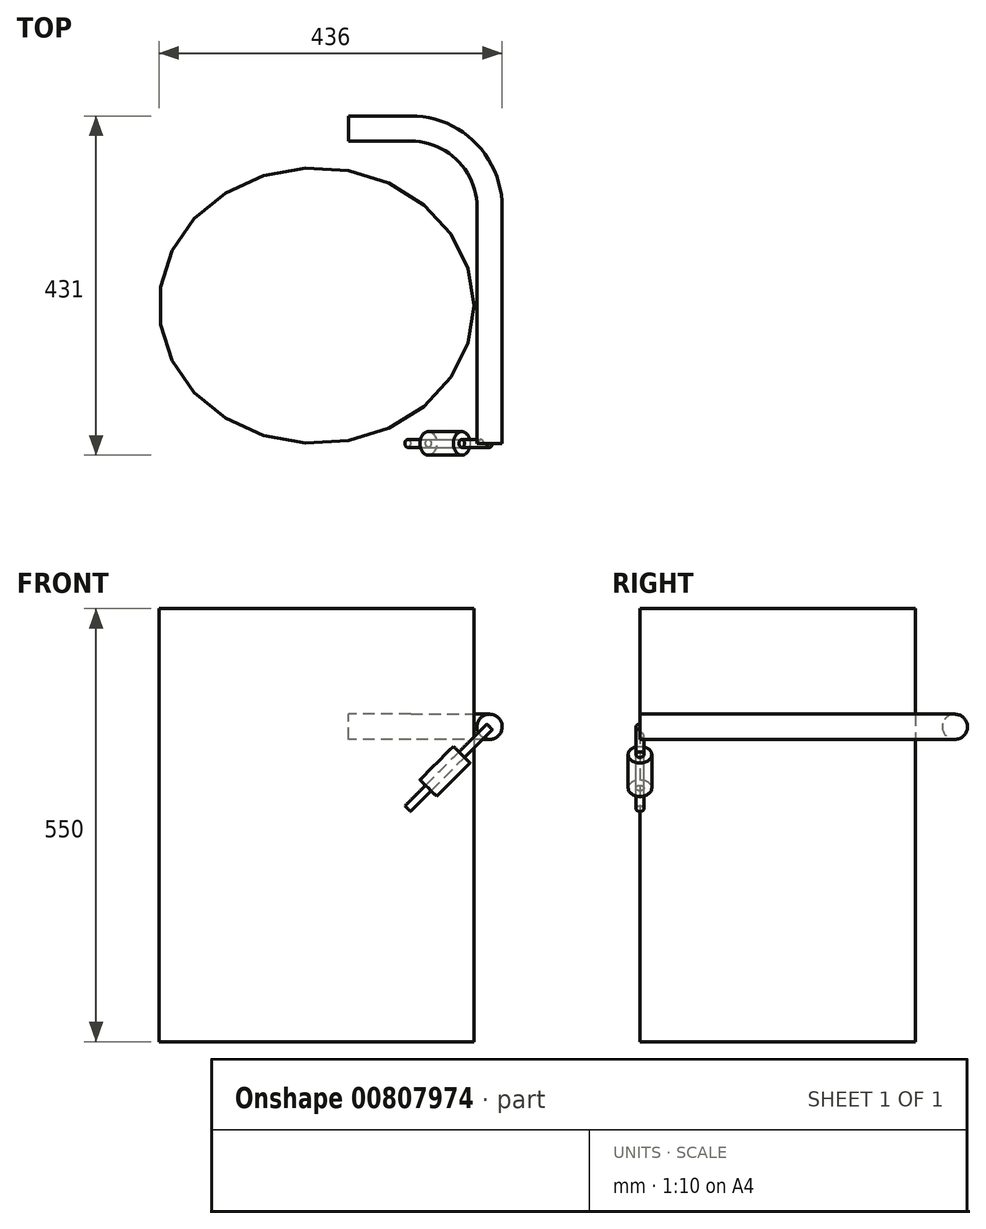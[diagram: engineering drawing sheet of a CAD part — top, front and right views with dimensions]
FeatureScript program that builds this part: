
annotation { "Feature Type Name" : "Feature", "Feature Type Description" : "" }
export const myFeature = defineFeature(function(context is Context, id is Id, definition is map)
    precondition{}
    {
        {
            var Q0;
            Q0=qCreatedBy(makeId("Top.planeOp"),FACE);
            var sketch = newSketch(context, id + "F0", { "sketchPlane" : qUnion([Q0])});
            skLineSegment(sketch, "E0", {"start": v(-179, 400) * mm, "end": v(-100, 400) * mm});
            skLineSegment(sketch, "E1", {"start": v(0, 0) * mm, "end": v(0, 300) * mm});
            skPoint(sketch, "E2.visualSharp", {"position": v(0, 400) * mm});
            skArc(sketch, "E2.filletArc", {"start": v(0, 300) * mm, "mid": v(-29.29, 370.71) * mm, "end": v(-100, 400) * mm});
            skSolve(sketch);
        }
        {
            var Q0;
            Q0=qCreatedBy(makeId("Front.planeOp"),FACE);
            var sketch = newSketch(context, id + "F1", { "sketchPlane" : qUnion([Q0])});
            skLineSegment(sketch, "E3", {"start": v(0, 0) * mm, "end": v(0, 117.2) * mm, "construction": true});
            skLineSegment(sketch, "E4", {"start": v(0, 0) * mm, "end": v(-104.01, -104.01) * mm});
            skSolve(sketch);
        }
        {
            var Q0;
            Q0=qCreatedBy(makeId("Front.planeOp"),FACE);
            var sketch = newSketch(context, id + "F2", { "sketchPlane" : qUnion([Q0])});
            skCircle(sketch, "E5", {"center": v(0, 0) * mm, "radius": 16 * mm});
            skSolve(sketch);
        }
        {
            var Q0;
            Q0=makeQuery(id+"F2.imprint","IMPRINT",FACE,{"disambiguationData":[TD([[makeQuery(id+"F2.imprint","IMPRINT",EDGE,{"derivedFrom":sQuery(id+"F2.wireOp",EDGE,"E5")}),1.0]])]});
            var Q1;
            Q1=sQuery(id+"F0.wireOp",EDGE,"E1");
            var Q2;
            Q2=sQuery(id+"F0.wireOp",EDGE,"E2.filletArc");
            var Q3;
            Q3=sQuery(id+"F0.wireOp",EDGE,"E0");
            sweep(context, id + "F3", {"profiles" : qUnion([Q0]), "path" : qUnion([Q1, Q2, Q3])});
        }
        {
            var Q0;
            Q0=sQuery(id+"F1.wireOp",EDGE,"E4");
            var Q1;
            Q1=sQuery(id+"F1.wireOp",VERTEX,"E3.start");
            cPlane(context, id + "F4", {"entities" : qUnion([Q0, Q1]), "cplaneType" : CPlaneType.LINE_POINT, "offset" : 25 * mm, "width" : 150 * mm, "height" : 150 * mm});
        }
        {
            var Q0;
            Q0=qCreatedBy(id+"F4.planeOp",FACE);
            var sketch = newSketch(context, id + "F5", { "sketchPlane" : qUnion([Q0])});
            skCircle(sketch, "E6", {"center": v(0, 0) * mm, "radius": 5 * mm});
            skSolve(sketch);
        }
        {
            var Q0;
            Q0 = qSketchRegion(id + "F5", true);
            var Q1;
            Q1=sQuery(id+"F1.wireOp",VERTEX,"E4.end");
            extrude(context, id + "F6", {"entities" : qUnion([Q0]), "operationType" : NewBodyOperationType.ADD, "endBound" : BoundingType.UP_TO_VERTEX, "depth" : 25 * mm, "endBoundEntityVertex" : qUnion([Q1]), "offsetDistance" : 25 * mm});
        }
        {
            var Q0;
            Q0=qCreatedBy(id+"F4.planeOp",FACE);
            cPlane(context, id + "F7", {"entities" : qUnion([Q0]), "cplaneType" : CPlaneType.OFFSET, "offset" : 50 * mm, "width" : 150 * mm, "height" : 150 * mm});
        }
        {
            var Q0;
            Q0=qCreatedBy(id+"F7.planeOp",FACE);
            var sketch = newSketch(context, id + "F8", { "sketchPlane" : qUnion([Q0])});
            skCircle(sketch, "E7", {"center": v(0, 0) * mm, "radius": 15 * mm});
            skCircle(sketch, "E8", {"center": v(0, 0) * mm, "radius": 5 * mm});
            skSolve(sketch);
        }
        {
            var Q0;
            Q0=makeQuery(id+"F8.imprint","IMPRINT",FACE,{"disambiguationData":[TD([[makeQuery(id+"F8.imprint","IMPRINT",EDGE,{"derivedFrom":sQuery(id+"F8.wireOp",EDGE,"E7")}),1.0]])]});
            extrude(context, id + "F9", {"entities" : qUnion([Q0]), "depth" : 60 * mm, "offsetDistance" : 25 * mm});
        }
        {
            var Q0;
            Q0=qCreatedBy(makeId("Top.planeOp"),FACE);
            var sketch = newSketch(context, id + "F10", { "sketchPlane" : qUnion([Q0])});
            skLineSegment(sketch, "E9", {"start": v(-220, 0) * mm, "end": v(-220, 350) * mm, "construction": true});
            skLineSegment(sketch, "E10", {"start": v(-420, 175) * mm, "end": v(-20, 175) * mm, "construction": true});
            skPoint(sketch, "E11", {"position": v(-220, 175) * mm});
            skPoint(sketch, "E11.positionSnap0", {"position": v(-220, 175) * mm});
            skEllipse(sketch, "E12", {"center": v(-220, 175) * mm, "majorRadius": 200 * mm, "minorRadius": 175 * mm, "majorAxis": v(1, 0)});
            skSolve(sketch);
        }
        {
            var Q0;
            Q0 = qSketchRegion(id + "F10", true);
            extrude(context, id + "F11", {"entities" : qUnion([Q0]), "depth" : 150 * mm, "offsetDistance" : 25 * mm, "hasSecondDirection" : true, "secondDirectionOppositeDirection" : true, "secondDirectionDepth" : 400 * mm});
        }
    });
